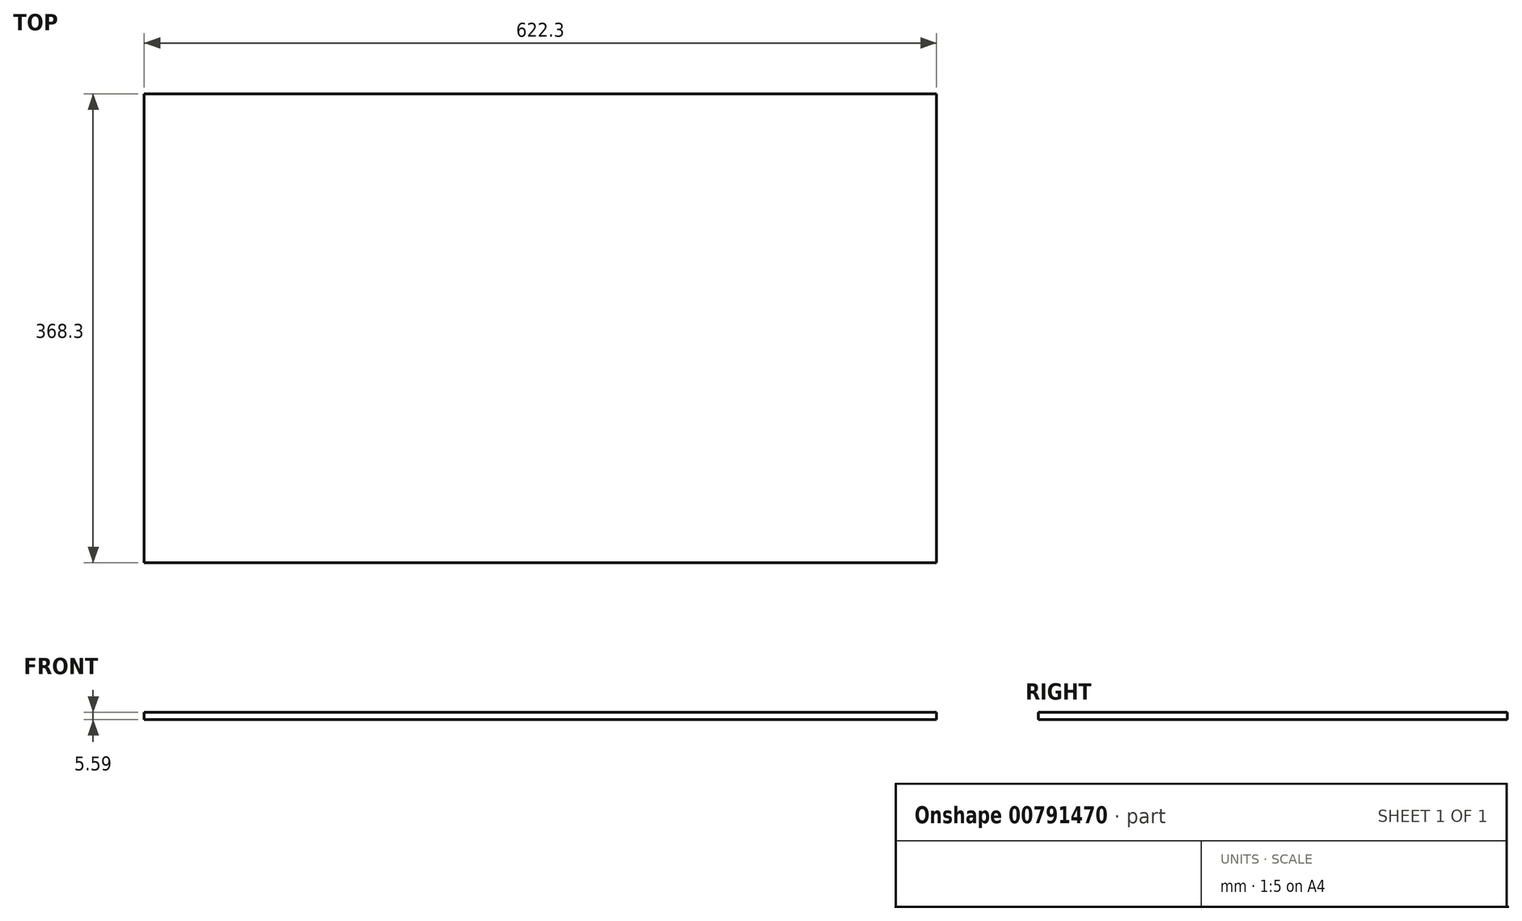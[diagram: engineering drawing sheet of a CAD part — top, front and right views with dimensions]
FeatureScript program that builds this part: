
annotation { "Feature Type Name" : "Feature", "Feature Type Description" : "" }
export const myFeature = defineFeature(function(context is Context, id is Id, definition is map)
    precondition{}
    {
        {
            var Q0;
            Q0=qCreatedBy(makeId("Top.planeOp"),FACE);
            var sketch = newSketch(context, id + "F0", { "sketchPlane" : qUnion([Q0])});
            skLineSegment(sketch, "E0.bottom", {"start": v(-311.15, 184.15) * mm, "end": v(311.15, 184.15) * mm});
            skLineSegment(sketch, "E0.top", {"start": v(-311.15, -184.15) * mm, "end": v(311.15, -184.15) * mm});
            skLineSegment(sketch, "E0.left", {"start": v(-311.15, 184.15) * mm, "end": v(-311.15, -184.15) * mm});
            skLineSegment(sketch, "E0.right", {"start": v(311.15, 184.15) * mm, "end": v(311.15, -184.15) * mm});
            skSolve(sketch);
        }
        {
            var Q0;
            Q0=makeQuery(id+"F0.imprint","IMPRINT",FACE,{"disambiguationData":[TD([[makeQuery(id+"F0.imprint","IMPRINT",EDGE,{"derivedFrom":sQuery(id+"F0.wireOp",EDGE,"E0.bottom")}),-1.0]])]});
            extrude(context, id + "F1", {"entities" : qUnion([Q0]), "depth" : 5.6 * mm, "offsetDistance" : 25.4 * mm});
        }
    });
